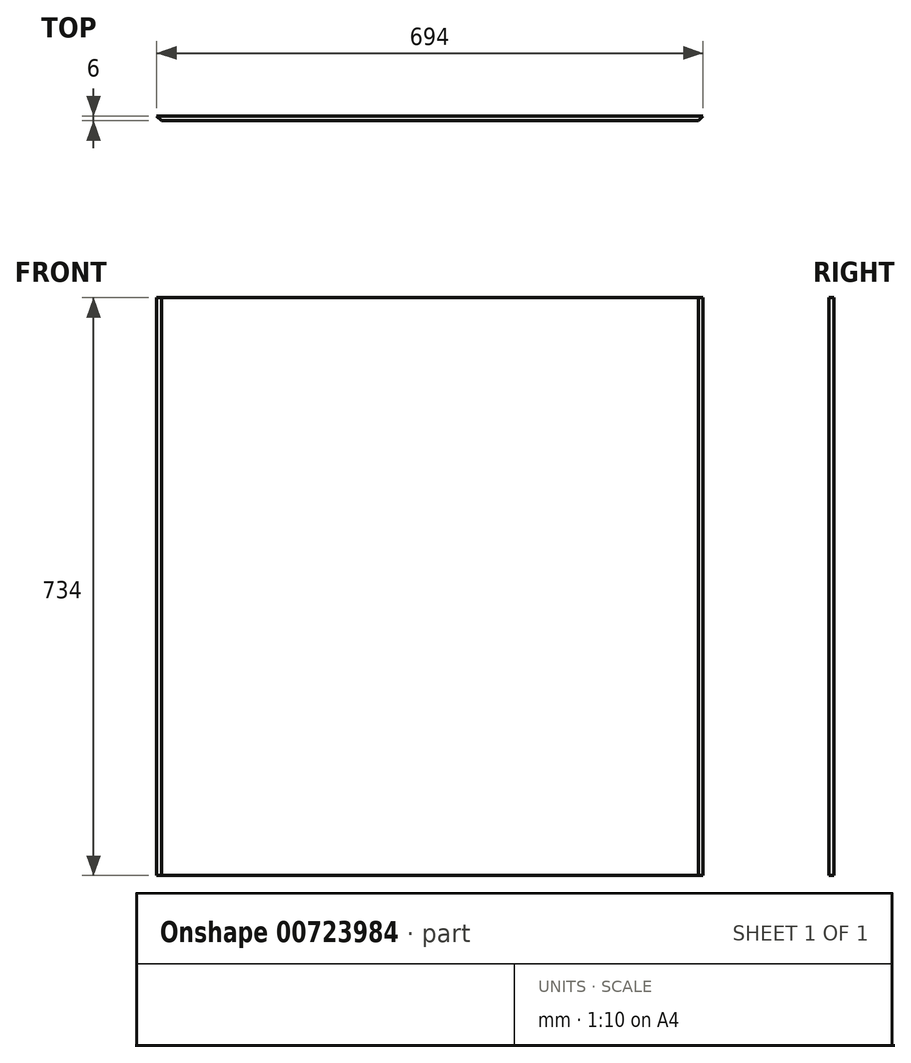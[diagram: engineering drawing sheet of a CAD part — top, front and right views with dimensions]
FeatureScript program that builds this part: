
annotation { "Feature Type Name" : "Feature", "Feature Type Description" : "" }
export const myFeature = defineFeature(function(context is Context, id is Id, definition is map)
    precondition{}
    {
        {
            var Q0;
            Q0=qCreatedBy(makeId("Front.planeOp"),FACE);
            var sketch = newSketch(context, id + "F0", { "sketchPlane" : qUnion([Q0])});
            skLineSegment(sketch, "E0.bottom", {"start": v(-347, 367) * mm, "end": v(347, 367) * mm});
            skLineSegment(sketch, "E0.top", {"start": v(-347, -367) * mm, "end": v(347, -367) * mm});
            skLineSegment(sketch, "E0.left", {"start": v(-347, 367) * mm, "end": v(-347, -367) * mm});
            skLineSegment(sketch, "E0.right", {"start": v(347, 367) * mm, "end": v(347, -367) * mm});
            skLineSegment(sketch, "E1", {"start": v(-347, 367) * mm, "end": v(347, -367) * mm, "construction": true});
            skSolve(sketch);
        }
        {
            var Q0;
            Q0=qSketchRegion(id+"F0",true);
            extrude(context, id + "F1", {"entities" : qUnion([Q0]), "depth" : 6 * mm, "offsetDistance" : 25 * mm});
        }
        {
            var Q0;
            Q0=makeQuery(id+"F1.opExtrude","CAP_EDGE",EDGE,{"disambiguationData":[OSD([sQuery(id+"F0.wireOp",EDGE,"E0.left")])],"isStart":false});
            var Q1;
            Q1=makeQuery(id+"F1.opExtrude","CAP_EDGE",EDGE,{"disambiguationData":[OSD([sQuery(id+"F0.wireOp",EDGE,"E0.right")])],"isStart":false});
            chamfer(context, id + "F2", {"entities" : qUnion([Q0, Q1]), "width" : 6 * mm, "tangentPropagation" : true});
        }
    });
